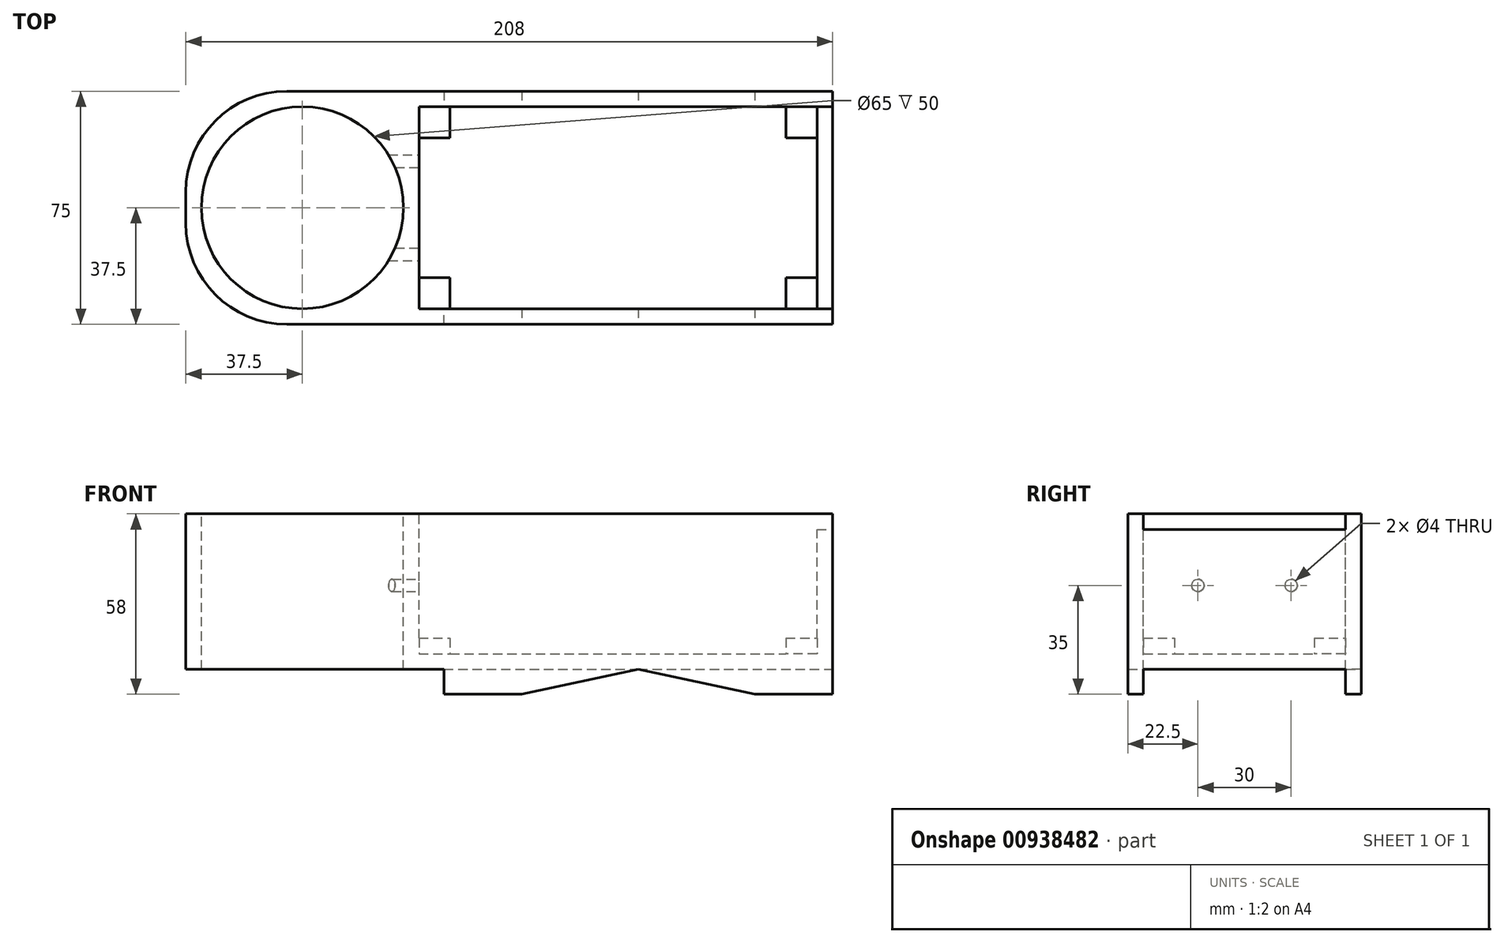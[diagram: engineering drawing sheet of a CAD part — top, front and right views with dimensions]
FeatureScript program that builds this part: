
annotation { "Feature Type Name" : "Feature", "Feature Type Description" : "" }
export const myFeature = defineFeature(function(context is Context, id is Id, definition is map)
    precondition{}
    {
        {
            var Q0;
            Q0=qCreatedBy(makeId("Front.planeOp"),FACE);
            var sketch = newSketch(context, id + "F0", { "sketchPlane" : qUnion([Q0])});
            skLineSegment(sketch, "E0.bottom", {"start": v(-104, -25) * mm, "end": v(104, -25) * mm});
            skLineSegment(sketch, "E0.top", {"start": v(-104, 25) * mm, "end": v(104, 25) * mm});
            skLineSegment(sketch, "E0.left", {"start": v(-104, -25) * mm, "end": v(-104, 25) * mm});
            skLineSegment(sketch, "E0.right", {"start": v(104, -25) * mm, "end": v(104, 25) * mm});
            skSolve(sketch);
        }
        {
            var Q0;
            Q0=makeQuery(id+"F0.imprint","IMPRINT",FACE,{"disambiguationData":[TD([[makeQuery(id+"F0.imprint","IMPRINT",EDGE,{"derivedFrom":sQuery(id+"F0.wireOp",EDGE,"E0.bottom")}),1.0]])]});
            extrude(context, id + "F1", {"entities" : qUnion([Q0]), "endBound" : BoundingType.SYMMETRIC, "oppositeDirection" : true, "depth" : 75 * mm, "offsetDistance" : 25.4 * mm});
        }
        {
            var Q0;
            Q0=makeQuery(id+"F1.opExtrude","SWEPT_FACE",FACE,{"disambiguationData":[OSD([sQuery(id+"F0.wireOp",EDGE,"E0.top")])]});
            var sketch = newSketch(context, id + "F2", { "sketchPlane" : qUnion([Q0])});
            skCircle(sketch, "E1", {"center": v(-66.5, 0) * mm, "radius": 32.5 * mm});
            skSolve(sketch);
        }
        {
            var Q0;
            Q0=makeQuery(id+"F2.imprint","IMPRINT",FACE,{"disambiguationData":[TD([[makeQuery(id+"F2.imprint","IMPRINT",EDGE,{"derivedFrom":sQuery(id+"F2.wireOp",EDGE,"E1")}),1.0]])]});
            extrude(context, id + "F3", {"entities" : qUnion([Q0]), "operationType" : NewBodyOperationType.REMOVE, "endBound" : BoundingType.THROUGH_ALL, "oppositeDirection" : true, "depth" : 25.4 * mm, "offsetDistance" : 25.4 * mm});
        }
        {
            var Q0;
            Q0=makeQuery(id+"F1.opExtrude","SWEPT_FACE",FACE,{"disambiguationData":[OSD([sQuery(id+"F0.wireOp",EDGE,"E0.top")])]});
            var sketch = newSketch(context, id + "F4", { "sketchPlane" : qUnion([Q0])});
            skLineSegment(sketch, "E2.bottom", {"start": v(-29, -32.5) * mm, "end": v(99, -32.5) * mm});
            skLineSegment(sketch, "E2.top", {"start": v(-29, 32.5) * mm, "end": v(99, 32.5) * mm});
            skLineSegment(sketch, "E2.left", {"start": v(-29, -32.5) * mm, "end": v(-29, 32.5) * mm});
            skLineSegment(sketch, "E2.right", {"start": v(99, -32.5) * mm, "end": v(99, 32.5) * mm});
            skSolve(sketch);
        }
        {
            var Q0;
            Q0=makeQuery(id+"F4.imprint","IMPRINT",FACE,{"disambiguationData":[TD([[makeQuery(id+"F4.imprint","IMPRINT",EDGE,{"derivedFrom":sQuery(id+"F4.wireOp",EDGE,"E2.bottom")}),1.0]])]});
            extrude(context, id + "F5", {"entities" : qUnion([Q0]), "operationType" : NewBodyOperationType.REMOVE, "oppositeDirection" : true, "depth" : 45 * mm, "offsetDistance" : 25.4 * mm});
        }
        {
            var Q0;
            Q0=makeQuery(id+"F1.opExtrude","SWEPT_FACE",FACE,{"disambiguationData":[OSD([sQuery(id+"F0.wireOp",EDGE,"E0.right")])]});
            var sketch = newSketch(context, id + "F6", { "sketchPlane" : qUnion([Q0])});
            skLineSegment(sketch, "E3.bottom", {"start": v(-32.5, 20) * mm, "end": v(32.5, 20) * mm});
            skLineSegment(sketch, "E3.top", {"start": v(-32.5, 25) * mm, "end": v(32.5, 25) * mm});
            skLineSegment(sketch, "E3.left", {"start": v(-32.5, 20) * mm, "end": v(-32.5, 25) * mm});
            skLineSegment(sketch, "E3.right", {"start": v(32.5, 20) * mm, "end": v(32.5, 25) * mm});
            skSolve(sketch);
        }
        {
            var Q0;
            Q0=makeQuery(id+"F6.imprint","IMPRINT",FACE,{"disambiguationData":[TD([[makeQuery(id+"F6.imprint","IMPRINT",EDGE,{"derivedFrom":sQuery(id+"F6.wireOp",EDGE,"E3.bottom")}),1.0]])]});
            extrude(context, id + "F7", {"entities" : qUnion([Q0]), "operationType" : NewBodyOperationType.REMOVE, "endBound" : BoundingType.UP_TO_NEXT, "oppositeDirection" : true, "depth" : 25.4 * mm, "offsetDistance" : 25.4 * mm});
        }
        {
            var Q0;
            Q0=makeQuery(id+"F5.boolean.opBoolean","COPY",FACE,{"derivedFrom":makeQuery(id+"F5.opExtrude","CAP_FACE",FACE,{"disambiguationData":[OSD([sQuery(id+"F4.wireOp",EDGE,"E2.bottom"),sQuery(id+"F4.wireOp",EDGE,"E2.top"),sQuery(id+"F4.wireOp",EDGE,"E2.left"),sQuery(id+"F4.wireOp",EDGE,"E2.right")])],"isStart":false})});
            var sketch = newSketch(context, id + "F8", { "sketchPlane" : qUnion([Q0])});
            skLineSegment(sketch, "E4.bottom", {"start": v(-29, -32.5) * mm, "end": v(-19, -32.5) * mm});
            skLineSegment(sketch, "E4.top", {"start": v(-29, -22.5) * mm, "end": v(-19, -22.5) * mm});
            skLineSegment(sketch, "E4.left", {"start": v(-29, -32.5) * mm, "end": v(-29, -22.5) * mm});
            skLineSegment(sketch, "E4.right", {"start": v(-19, -32.5) * mm, "end": v(-19, -22.5) * mm});
            skLineSegment(sketch, "E5.bottom", {"start": v(-29, 32.5) * mm, "end": v(-19, 32.5) * mm});
            skLineSegment(sketch, "E5.top", {"start": v(-29, 22.5) * mm, "end": v(-19, 22.5) * mm});
            skLineSegment(sketch, "E5.left", {"start": v(-29, 32.5) * mm, "end": v(-29, 22.5) * mm});
            skLineSegment(sketch, "E5.right", {"start": v(-19, 32.5) * mm, "end": v(-19, 22.5) * mm});
            skLineSegment(sketch, "E6.bottom", {"start": v(99, 32.5) * mm, "end": v(89, 32.5) * mm});
            skLineSegment(sketch, "E6.top", {"start": v(99, 22.5) * mm, "end": v(89, 22.5) * mm});
            skLineSegment(sketch, "E6.left", {"start": v(99, 32.5) * mm, "end": v(99, 22.5) * mm});
            skLineSegment(sketch, "E6.right", {"start": v(89, 32.5) * mm, "end": v(89, 22.5) * mm});
            skLineSegment(sketch, "E7.bottom", {"start": v(99, -32.5) * mm, "end": v(89, -32.5) * mm});
            skLineSegment(sketch, "E7.top", {"start": v(99, -22.5) * mm, "end": v(89, -22.5) * mm});
            skLineSegment(sketch, "E7.left", {"start": v(99, -32.5) * mm, "end": v(99, -22.5) * mm});
            skLineSegment(sketch, "E7.right", {"start": v(89, -32.5) * mm, "end": v(89, -22.5) * mm});
            skSolve(sketch);
        }
        {
            var Q0;
            Q0=makeQuery(id+"F8.imprint","IMPRINT",FACE,{"disambiguationData":[TD([[makeQuery(id+"F8.imprint","IMPRINT",EDGE,{"derivedFrom":sQuery(id+"F8.wireOp",EDGE,"E5.bottom")}),-1.0]])]});
            var Q1;
            Q1=makeQuery(id+"F8.imprint","IMPRINT",FACE,{"disambiguationData":[TD([[makeQuery(id+"F8.imprint","IMPRINT",EDGE,{"derivedFrom":sQuery(id+"F8.wireOp",EDGE,"E6.bottom")}),-1.0]])]});
            var Q2;
            Q2=makeQuery(id+"F8.imprint","IMPRINT",FACE,{"disambiguationData":[TD([[makeQuery(id+"F8.imprint","IMPRINT",EDGE,{"derivedFrom":sQuery(id+"F8.wireOp",EDGE,"E4.bottom")}),1.0]])]});
            var Q3;
            Q3=makeQuery(id+"F8.imprint","IMPRINT",FACE,{"disambiguationData":[TD([[makeQuery(id+"F8.imprint","IMPRINT",EDGE,{"derivedFrom":sQuery(id+"F8.wireOp",EDGE,"E7.bottom")}),1.0]])]});
            extrude(context, id + "F9", {"entities" : qUnion([Q0, Q1, Q2, Q3]), "operationType" : NewBodyOperationType.ADD, "depth" : 5 * mm, "offsetDistance" : 25.4 * mm});
        }
        {
            var Q0;
            Q0=makeQuery(id+"F5.boolean.opBoolean","COPY",FACE,{"derivedFrom":makeQuery(id+"F5.opExtrude","SWEPT_FACE",FACE,{"disambiguationData":[OSD([sQuery(id+"F4.wireOp",EDGE,"E2.left")])]})});
            var sketch = newSketch(context, id + "F10", { "sketchPlane" : qUnion([Q0])});
            skCircle(sketch, "E8", {"center": v(-15, 2) * mm, "radius": 2 * mm});
            skCircle(sketch, "E9", {"center": v(15, 2) * mm, "radius": 2 * mm});
            skSolve(sketch);
        }
        {
            var Q0;
            Q0=makeQuery(id+"F10.imprint","IMPRINT",FACE,{"disambiguationData":[TD([[makeQuery(id+"F10.imprint","IMPRINT",EDGE,{"derivedFrom":sQuery(id+"F10.wireOp",EDGE,"E8")}),1.0]])]});
            var Q1;
            Q1=makeQuery(id+"F10.imprint","IMPRINT",FACE,{"disambiguationData":[TD([[makeQuery(id+"F10.imprint","IMPRINT",EDGE,{"derivedFrom":sQuery(id+"F10.wireOp",EDGE,"E9")}),1.0]])]});
            extrude(context, id + "F11", {"entities" : qUnion([Q0, Q1]), "operationType" : NewBodyOperationType.REMOVE, "endBound" : BoundingType.UP_TO_NEXT, "oppositeDirection" : true, "depth" : 25.4 * mm, "offsetDistance" : 25.4 * mm});
        }
        {
            var Q0;
            Q0=makeQuery(id+"F1.opExtrude","CAP_EDGE",EDGE,{"disambiguationData":[OSD([sQuery(id+"F0.wireOp",EDGE,"E0.left")])],"isStart":true});
            var Q1;
            Q1=makeQuery(id+"F1.opExtrude","CAP_EDGE",EDGE,{"disambiguationData":[OSD([sQuery(id+"F0.wireOp",EDGE,"E0.left")])],"isStart":false});
            fillet(context, id + "F12", {"entities" : qUnion([Q0, Q1]), "radius" : 32.5 * mm, "tangentPropagation" : true, "allowEdgeOverflow" : false});
        }
        {
            var Q0;
            Q0=makeQuery(id+"F1.opExtrude","SWEPT_FACE",FACE,{"disambiguationData":[OSD([sQuery(id+"F0.wireOp",EDGE,"E0.bottom")])]});
            var sketch = newSketch(context, id + "F13", { "sketchPlane" : qUnion([Q0])});
            skLineSegment(sketch, "E10.bottom", {"start": v(-21, -37.5) * mm, "end": v(104, -37.5) * mm});
            skLineSegment(sketch, "E10.top", {"start": v(-21, -32.5) * mm, "end": v(104, -32.5) * mm});
            skLineSegment(sketch, "E10.left", {"start": v(-21, -37.5) * mm, "end": v(-21, -32.5) * mm});
            skLineSegment(sketch, "E10.right", {"start": v(104, -37.5) * mm, "end": v(104, -32.5) * mm});
            skLineSegment(sketch, "E11.bottom", {"start": v(-21, 37.5) * mm, "end": v(104, 37.5) * mm});
            skLineSegment(sketch, "E11.top", {"start": v(-21, 32.5) * mm, "end": v(104, 32.5) * mm});
            skLineSegment(sketch, "E11.left", {"start": v(-21, 37.5) * mm, "end": v(-21, 32.5) * mm});
            skLineSegment(sketch, "E11.right", {"start": v(104, 37.5) * mm, "end": v(104, 32.5) * mm});
            skSolve(sketch);
        }
        {
            var Q0;
            Q0=makeQuery(id+"F13.imprint","IMPRINT",FACE,{"disambiguationData":[TD([[makeQuery(id+"F13.imprint","IMPRINT",EDGE,{"derivedFrom":sQuery(id+"F13.wireOp",EDGE,"E11.bottom")}),-1.0]])]});
            var Q1;
            Q1=makeQuery(id+"F13.imprint","IMPRINT",FACE,{"disambiguationData":[TD([[makeQuery(id+"F13.imprint","IMPRINT",EDGE,{"derivedFrom":sQuery(id+"F13.wireOp",EDGE,"E10.bottom")}),1.0]])]});
            extrude(context, id + "F14", {"entities" : qUnion([Q0, Q1]), "operationType" : NewBodyOperationType.ADD, "depth" : 8 * mm, "offsetDistance" : 25.4 * mm});
        }
        {
            var Q0;
            Q0=makeQuery(id+"F14.boolean.opBoolean","MERGE",FACE,{"derivedFrom":[makeQuery(id+"F1.opExtrude","CAP_FACE",FACE,{"disambiguationData":[OSD([sQuery(id+"F0.wireOp",EDGE,"E0.bottom"),sQuery(id+"F0.wireOp",EDGE,"E0.top"),sQuery(id+"F0.wireOp",EDGE,"E0.left"),sQuery(id+"F0.wireOp",EDGE,"E0.right")])],"isStart":true}),makeQuery(id+"F14.opExtrude","SWEPT_FACE",FACE,{"disambiguationData":[OSD([sQuery(id+"F13.wireOp",EDGE,"E11.bottom")])]})]});
            var sketch = newSketch(context, id + "F15", { "sketchPlane" : qUnion([Q0])});
            skLineSegment(sketch, "E12", {"start": v(4, -33) * mm, "end": v(41.5, -25) * mm});
            skLineSegment(sketch, "E13", {"start": v(41.5, -25) * mm, "end": v(79, -33) * mm});
            skLineSegment(sketch, "E14", {"start": v(4, -33) * mm, "end": v(79, -33) * mm});
            skSolve(sketch);
        }
        {
            var Q0;
            Q0=makeQuery(id+"F15.imprint","IMPRINT",FACE,{"disambiguationData":[TD([[makeQuery(id+"F15.imprint","IMPRINT",EDGE,{"derivedFrom":sQuery(id+"F15.wireOp",EDGE,"E12")}),-1.0]])]});
            extrude(context, id + "F16", {"entities" : qUnion([Q0]), "operationType" : NewBodyOperationType.REMOVE, "endBound" : BoundingType.THROUGH_ALL, "oppositeDirection" : true, "depth" : 25.4 * mm, "offsetDistance" : 25.4 * mm});
        }
    });
